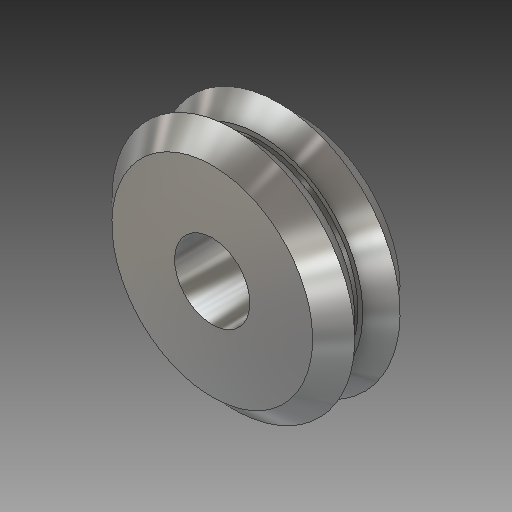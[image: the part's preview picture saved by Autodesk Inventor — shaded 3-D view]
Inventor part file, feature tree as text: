
AUTODESK INVENTOR PART (.ipt)
format: ipt  version: 2017 SP1 (Build 210196100, 196)  size: 174,080 bytes
history: native  units: in
note: dims shown in document units (in); Inventor stores cm internally (conversion verified against a paired STEP export)
features: revolve x1, sketch x1
ambient origin geometry x8: Origin, YZ Plane, XZ Plane, XY Plane, X Axis, Y Axis, Z Axis, Center Point
bodies: Solid1 (feature_tree)
feature tree (2):
  revolve  "Revolution1"  [1 undecoded]
  sketch  "Sketch1"  dims[d0=0.1875in d1=0.5in d3=0.04in d4=0.436in d5=90.0deg d6=0.605in d7=0.226in]
note: 1 required parameter value undecoded (feature->parameter linkage not recoverable at this tier; creation-order binding heuristic only, values carry confidence <= 0.55)
